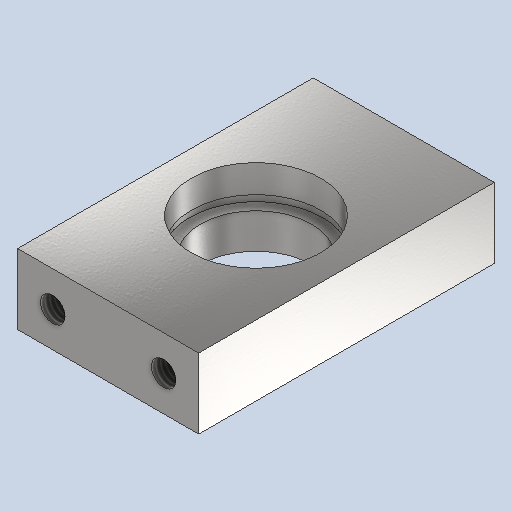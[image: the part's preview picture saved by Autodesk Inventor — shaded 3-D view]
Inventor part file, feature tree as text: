
AUTODESK INVENTOR PART (.ipt)
format: ipt  version: 2024 (Build 280153000, 153)  size: 331,776 bytes
history: native  units: mm
features: hole x4, sketch x4, extrude x1, plane x1
ambient origin geometry x8: Origin, YZ Plane, XZ Plane, XY Plane, X Axis, Y Axis, Z Axis, Center Point
bodies: Volumenkörper1 (feature_tree)
feature tree (10):
  extrude  "Extrusion1"  Depth=80.0mm
  hole  "Bohrung1"  [1 undecoded]
  hole  "Bohrung2"  [1 undecoded]
  plane  "Arbeitsebene1"
  sketch  "Skizze6"  dims[d12=35.0mm d13=6.647mm d14=16.0mm d15=4.0mm d16=2.0mm d17=90.0deg d18=22.2mm d19=20.594885mm d20=9.5mm d21=30.0mm d30=9.5mm d31=35.0mm d32=16.0mm d33=36.0mm d34=2.0mm d35=90.0deg d36=22.2mm d37=0.0mm d38=30.0mm d39=6.0mm d40=36.0mm d41=2.0mm d42=90.0deg d43=8.0mm d44=0.0mm]
  hole  "Bohrung4"  [1 undecoded]
  hole  "Bohrung5"  [1 undecoded]
  sketch  "Skizze1"  dims[d0=49.0mm d1=80.0mm]
  sketch  "Skizze2"  dims[d2=19.0mm d3=0.0mm]
  sketch  "Skizze3"  dims[d4=4.917mm d5=12.0mm d6=4.0mm d7=2.0mm d8=90.0deg d9=17.1mm d10=20.594885mm d11=7.0mm]
note: 4 required parameter values undecoded (feature->parameter linkage not recoverable at this tier; creation-order binding heuristic only, values carry confidence <= 0.55)
